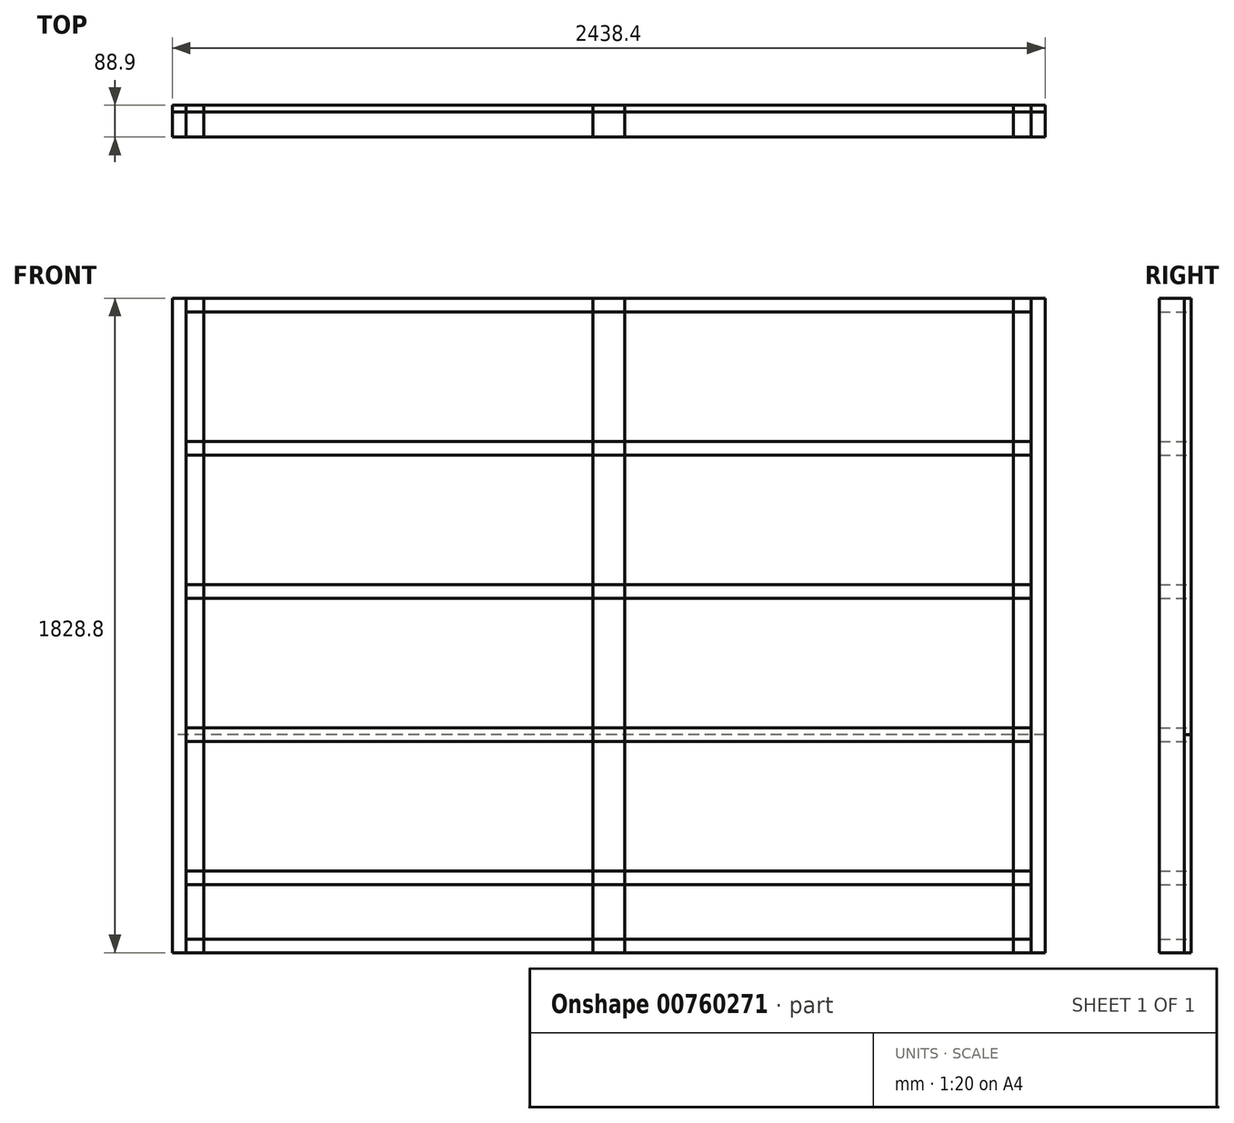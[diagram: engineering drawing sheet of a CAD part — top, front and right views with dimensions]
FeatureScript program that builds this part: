
annotation { "Feature Type Name" : "Feature", "Feature Type Description" : "" }
export const myFeature = defineFeature(function(context is Context, id is Id, definition is map)
    precondition{}
    {
        {
            var Q0;
            Q0=qCreatedBy(makeId("Front.planeOp"),FACE);
            var sketch = newSketch(context, id + "F0", { "sketchPlane" : qUnion([Q0])});
            skLineSegment(sketch, "E0.bottom", {"start": v(-1219.2, 914.4) * mm, "end": v(1219.2, 914.4) * mm});
            skLineSegment(sketch, "E0.top", {"start": v(-1219.2, -914.4) * mm, "end": v(1219.2, -914.4) * mm});
            skLineSegment(sketch, "E0.left", {"start": v(-1219.2, 914.4) * mm, "end": v(-1219.2, -914.4) * mm});
            skLineSegment(sketch, "E0.right", {"start": v(1219.2, 914.4) * mm, "end": v(1219.2, -914.4) * mm});
            skPoint(sketch, "E0.middle", {"position": v(0, 0) * mm});
            skSolve(sketch);
        }
        {
            var Q0;
            Q0=makeQuery(id+"F0.imprint","IMPRINT",FACE,{"disambiguationData":[TD([[makeQuery(id+"F0.imprint","IMPRINT",EDGE,{"derivedFrom":sQuery(id+"F0.wireOp",EDGE,"E0.bottom")}),-1.0]])]});
            var sketch = newSketch(context, id + "F1", { "sketchPlane" : qUnion([Q0])});
            skLineSegment(sketch, "E1.bottom", {"start": v(-1219.2, 914.4) * mm, "end": v(-1130.3, 914.4) * mm});
            skLineSegment(sketch, "E1.top", {"start": v(-1219.2, -914.4) * mm, "end": v(-1130.3, -914.4) * mm});
            skLineSegment(sketch, "E1.left", {"start": v(-1219.2, 914.4) * mm, "end": v(-1219.2, -914.4) * mm});
            skLineSegment(sketch, "E1.right", {"start": v(-1130.3, 914.4) * mm, "end": v(-1130.3, -914.4) * mm});
            skLineSegment(sketch, "E2.bottom", {"start": v(1130.3, 914.4) * mm, "end": v(1219.2, 914.4) * mm});
            skLineSegment(sketch, "E2.top", {"start": v(1130.3, -914.4) * mm, "end": v(1219.2, -914.4) * mm});
            skLineSegment(sketch, "E2.left", {"start": v(1130.3, 914.4) * mm, "end": v(1130.3, -914.4) * mm});
            skLineSegment(sketch, "E2.right", {"start": v(1219.2, 914.4) * mm, "end": v(1219.2, -914.4) * mm});
            skLineSegment(sketch, "E3.bottom", {"start": v(-44.45, 914.4) * mm, "end": v(44.45, 914.4) * mm});
            skLineSegment(sketch, "E3.top", {"start": v(-44.45, -914.4) * mm, "end": v(44.45, -914.4) * mm});
            skLineSegment(sketch, "E3.left", {"start": v(-44.45, 914.4) * mm, "end": v(-44.45, -914.4) * mm});
            skLineSegment(sketch, "E3.right", {"start": v(44.45, 914.4) * mm, "end": v(44.45, -914.4) * mm});
            skSolve(sketch);
        }
        {
            var Q0;
            Q0=makeQuery(id+"F0.imprint","IMPRINT",FACE,{"disambiguationData":[TD([[makeQuery(id+"F0.imprint","IMPRINT",EDGE,{"derivedFrom":sQuery(id+"F0.wireOp",EDGE,"E0.bottom")}),-1.0]])]});
            var sketch = newSketch(context, id + "F2", { "sketchPlane" : qUnion([Q0])});
            skLineSegment(sketch, "E4.bottom", {"start": v(-1181.1, 914.4) * mm, "end": v(1181.1, 914.4) * mm});
            skLineSegment(sketch, "E4.top", {"start": v(-1181.1, 876.3) * mm, "end": v(1181.1, 876.3) * mm});
            skLineSegment(sketch, "E4.left", {"start": v(-1181.1, 914.4) * mm, "end": v(-1181.1, 876.3) * mm});
            skLineSegment(sketch, "E4.right", {"start": v(1181.1, 914.4) * mm, "end": v(1181.1, 876.3) * mm});
            skLineSegment(sketch, "E5.bottom", {"start": v(-1181.1, -876.3) * mm, "end": v(1181.1, -876.3) * mm});
            skLineSegment(sketch, "E5.top", {"start": v(-1181.1, -914.4) * mm, "end": v(1181.1, -914.4) * mm});
            skLineSegment(sketch, "E5.left", {"start": v(-1181.1, -876.3) * mm, "end": v(-1181.1, -914.4) * mm});
            skLineSegment(sketch, "E5.right", {"start": v(1181.1, -876.3) * mm, "end": v(1181.1, -914.4) * mm});
            skLineSegment(sketch, "E6.bottom", {"start": v(1219.2, 914.4) * mm, "end": v(1181.1, 914.4) * mm});
            skLineSegment(sketch, "E6.top", {"start": v(1219.2, -914.4) * mm, "end": v(1181.1, -914.4) * mm});
            skLineSegment(sketch, "E6.left", {"start": v(1219.2, 914.4) * mm, "end": v(1219.2, -914.4) * mm});
            skLineSegment(sketch, "E6.right", {"start": v(1181.1, 914.4) * mm, "end": v(1181.1, -914.4) * mm});
            skLineSegment(sketch, "E7.bottom", {"start": v(-1219.2, 914.4) * mm, "end": v(-1181.1, 914.4) * mm});
            skLineSegment(sketch, "E7.top", {"start": v(-1219.2, -914.4) * mm, "end": v(-1181.1, -914.4) * mm});
            skLineSegment(sketch, "E7.left", {"start": v(-1219.2, 914.4) * mm, "end": v(-1219.2, -914.4) * mm});
            skLineSegment(sketch, "E7.right", {"start": v(-1181.1, 914.4) * mm, "end": v(-1181.1, -914.4) * mm});
            skLineSegment(sketch, "E8.0.1.0", {"start": v(-1181.1, 476.25) * mm, "end": v(1181.1, 476.25) * mm});
            skLineSegment(sketch, "E8.0.1.1", {"start": v(-1181.1, 514.35) * mm, "end": v(1181.1, 514.35) * mm});
            skLineSegment(sketch, "E8.0.2.0", {"start": v(-1181.1, 76.2) * mm, "end": v(1181.1, 76.2) * mm});
            skLineSegment(sketch, "E8.0.2.1", {"start": v(-1181.1, 114.3) * mm, "end": v(1181.1, 114.3) * mm});
            skLineSegment(sketch, "E8.0.3.0", {"start": v(-1181.1, -323.85) * mm, "end": v(1181.1, -323.85) * mm});
            skLineSegment(sketch, "E8.0.3.1", {"start": v(-1181.1, -285.75) * mm, "end": v(1181.1, -285.75) * mm});
            skLineSegment(sketch, "E8.direction1", {"start": v(-1181.1, 876.3) * mm, "end": v(-945.05, 876.3) * mm, "construction": true});
            skLineSegment(sketch, "E8.direction2", {"start": v(-1181.1, 876.3) * mm, "end": v(-1181.1, 476.25) * mm, "construction": true});
            skPoint(sketch, "E9", {"position": v(-1181.1, -304.8) * mm});
            skLineSegment(sketch, "E10.0.0.4", {"start": v(-1181.1, -723.9) * mm, "end": v(1181.1, -723.9) * mm});
            skLineSegment(sketch, "E10.3.0.4", {"start": v(-1181.1, -685.8) * mm, "end": v(1181.1, -685.8) * mm});
            skSolve(sketch);
        }
        {
            var Q0;
            Q0=makeQuery(id+"F1.imprint","IMPRINT",FACE,{"disambiguationData":[TD([[makeQuery(id+"F1.imprint","IMPRINT",EDGE,{"derivedFrom":sQuery(id+"F1.wireOp",EDGE,"E1.bottom")}),-1.0]])]});
            var Q1;
            Q1=makeQuery(id+"F1.imprint","IMPRINT",FACE,{"disambiguationData":[TD([[makeQuery(id+"F1.imprint","IMPRINT",EDGE,{"derivedFrom":sQuery(id+"F1.wireOp",EDGE,"E3.bottom")}),-1.0]])]});
            var Q2;
            Q2=makeQuery(id+"F1.imprint","IMPRINT",FACE,{"disambiguationData":[TD([[makeQuery(id+"F1.imprint","IMPRINT",EDGE,{"derivedFrom":sQuery(id+"F1.wireOp",EDGE,"E2.bottom")}),-1.0]])]});
            extrude(context, id + "F3", {"entities" : qUnion([Q0, Q1, Q2]), "depth" : 88.9 * mm, "offsetDistance" : 25.4 * mm});
        }
        {
            var Q0;
            {var subQ0=sQuery(id+"F2.wireOp",EDGE,"E4.bottom");Q0=makeQuery(id+"F2.imprint","IMPRINT",FACE,{"disambiguationData":[TD([[makeQuery(id+"F2.imprint","IMPRINT",EDGE,{"derivedFrom":subQ0}),-1.0]])]});}
            var Q1;
            {var subQ0=sQuery(id+"F2.wireOp",EDGE,"E5.bottom");Q1=makeQuery(id+"F2.imprint","IMPRINT",FACE,{"disambiguationData":[TD([[makeQuery(id+"F2.imprint","IMPRINT",EDGE,{"derivedFrom":subQ0}),-1.0]])]});}
            extrude(context, id + "F4", {"entities" : qUnion([Q0, Q1]), "depth" : 88.9 * mm, "offsetDistance" : 25.4 * mm});
        }
        {
            var Q0;
            {var subQ1=sQuery(id+"F2.wireOp",EDGE,"E7.bottom");Q0=makeQuery(id+"F2.imprint","IMPRINT",FACE,{"disambiguationData":[TD([[makeQuery(id+"F2.imprint","IMPRINT",EDGE,{"derivedFrom":subQ1}),-1.0]])]});}
            var Q1;
            {var subQ1=sQuery(id+"F2.wireOp",EDGE,"E6.bottom");Q1=makeQuery(id+"F2.imprint","IMPRINT",FACE,{"disambiguationData":[TD([[makeQuery(id+"F2.imprint","IMPRINT",EDGE,{"derivedFrom":subQ1}),-1.0]])]});}
            extrude(context, id + "F5", {"entities" : qUnion([Q0, Q1]), "depth" : 88.9 * mm, "offsetDistance" : 25.4 * mm});
        }
        {
            var Q0;
            {var subQ0=sQuery(id+"F2.wireOp",EDGE,"E8.0.1.0");Q0=makeQuery(id+"F2.imprint","IMPRINT",FACE,{"disambiguationData":[TD([[makeQuery(id+"F2.imprint","IMPRINT",EDGE,{"derivedFrom":subQ0}),1.0]])]});}
            var Q1;
            {var subQ0=sQuery(id+"F2.wireOp",EDGE,"E8.0.2.0");Q1=makeQuery(id+"F2.imprint","IMPRINT",FACE,{"disambiguationData":[TD([[makeQuery(id+"F2.imprint","IMPRINT",EDGE,{"derivedFrom":subQ0}),1.0]])]});}
            var Q2;
            {var subQ0=sQuery(id+"F2.wireOp",EDGE,"E8.0.3.0");Q2=makeQuery(id+"F2.imprint","IMPRINT",FACE,{"disambiguationData":[TD([[makeQuery(id+"F2.imprint","IMPRINT",EDGE,{"derivedFrom":subQ0}),1.0]])]});}
            var Q3;
            {var subQ0=sQuery(id+"F2.wireOp",EDGE,"E8.0.4.0");Q3=makeQuery(id+"F2.imprint","IMPRINT",FACE,{"disambiguationData":[TD([[makeQuery(id+"F2.imprint","IMPRINT",EDGE,{"derivedFrom":subQ0}),1.0]])]});}
            extrude(context, id + "F6", {"entities" : qUnion([Q0, Q1, Q2, Q3]), "depth" : 88.9 * mm, "offsetDistance" : 25.4 * mm});
        }
        {
            var Q0;
            {var subQ0=sQuery(id+"F2.wireOp",EDGE,"E8.0.1.0");Q0=makeQuery(id+"F2.imprint","IMPRINT",FACE,{"disambiguationData":[TD([[makeQuery(id+"F2.imprint","IMPRINT",EDGE,{"derivedFrom":subQ0}),-1.0]])]});}
            var sketch = newSketch(context, id + "F7", { "sketchPlane" : qUnion([Q0])});
            skLineSegment(sketch, "E11.bottom", {"start": v(1219.2, 914.4) * mm, "end": v(-1219.2, 914.4) * mm});
            skLineSegment(sketch, "E11.top", {"start": v(1219.2, -304.8) * mm, "end": v(-1219.2, -304.8) * mm});
            skLineSegment(sketch, "E11.left", {"start": v(1219.2, 914.4) * mm, "end": v(1219.2, -304.8) * mm});
            skLineSegment(sketch, "E11.right", {"start": v(-1219.2, 914.4) * mm, "end": v(-1219.2, -304.8) * mm});
            skLineSegment(sketch, "E12.top", {"start": v(1219.2, -914.4) * mm, "end": v(-1219.2, -914.4) * mm});
            skLineSegment(sketch, "E12.left", {"start": v(1219.2, -304.8) * mm, "end": v(1219.2, -914.4) * mm});
            skLineSegment(sketch, "E12.right", {"start": v(-1219.2, -304.8) * mm, "end": v(-1219.2, -914.4) * mm});
            skSolve(sketch);
        }
        {
            var Q0;
            {var subQ0=sQuery(id+"F2.wireOp",EDGE,"E8.0.3.0");Q0=makeQuery(id+"F2.imprint","IMPRINT",FACE,{"disambiguationData":[TD([[makeQuery(id+"F2.imprint","IMPRINT",EDGE,{"derivedFrom":subQ0}),1.0]])]});}
            var Q1;
            {var subQ0=sQuery(id+"F2.wireOp",EDGE,"E10.0.0.4");Q1=makeQuery(id+"F2.imprint","IMPRINT",FACE,{"disambiguationData":[TD([[makeQuery(id+"F2.imprint","IMPRINT",EDGE,{"derivedFrom":subQ0}),1.0]])]});}
            extrude(context, id + "F8", {"entities" : qUnion([Q0, Q1]), "depth" : 88.9 * mm, "offsetDistance" : 25.4 * mm});
        }
        {
            var Q0;
            Q0=makeQuery(id+"F7.imprint","IMPRINT",FACE,{"disambiguationData":[TD([[makeQuery(id+"F7.imprint","IMPRINT",EDGE,{"derivedFrom":sQuery(id+"F7.wireOp",EDGE,"E11.bottom")}),1.0]])]});
            var Q1;
            {var subQ0=sQuery(id+"F2.wireOp",EDGE,"E8.0.1.0");Q1=makeQuery(id+"F7.imprint","IMPRINT",FACE,{"disambiguationData":[TD([[makeQuery(id+"F7.imprint","IMPRINT",EDGE,{"derivedFrom":makeQuery(id+"F2.imprint","IMPRINT",EDGE,{"derivedFrom":subQ0})}),-1.0]])]});}
            extrude(context, id + "F9", {"entities" : qUnion([Q0, Q1]), "depth" : 19.05 * mm, "offsetDistance" : 25.4 * mm});
        }
        {
            var Q0;
            Q0=makeQuery(id+"F7.imprint","IMPRINT",FACE,{"disambiguationData":[TD([[makeQuery(id+"F7.imprint","IMPRINT",EDGE,{"derivedFrom":sQuery(id+"F7.wireOp",EDGE,"E11.top")}),1.0]])]});
            extrude(context, id + "F10", {"entities" : qUnion([Q0]), "depth" : 19.05 * mm, "offsetDistance" : 25.4 * mm});
        }
    });
